# Revit family: Sanitary_Accessories_DURAVIT-AG_DuraSystem-Electronic-flush-plate-for-WC
name_source: partatom
category: Generic Models
revit_build: Autodesk Revit 2018 (Build: 20180329_1100(x64)
units: mm (PartAtom-declared; Revit-internal decimal feet)

## family parameters
Can host rebar = No
Cut with Voids When Loaded = No
Host = Face
OmniClass Number = 23.19.31.17
OmniClass Title = Sanitary Room Units
Part Type = Normal
Room Calculation Point = No
Round Connector Dimension = Use Diameter
Shared = No

## types (1)
- DuraSystem Electronic flush plate for WC 230x10x157 mm - WD5003
    BIMobject category = Bathroom Accessories
    Connector Description = Power input
    Date of publishing = 26.05.2020 00:00:00
    Default Elevation = 1219 mm
    Description = Duravit DuraSystem Electronic flush plate for WC 230x10x157 mm - WD5003012000
    Design country = Germany
    EAN code = 4053424507316
    ETIM classification = EC012353 | Accessories bathroom accessories
    Edition number = 1
    IFC Classification = Furnishing Element
    Installation instructions = https://pro.duravit.com
    Main material = Duravit - Metal - 00 - White Alpin
    Manufacturer = Duravit
    Manufacturer country = Germany
    Manufacturer name = DURAVIT AG
    Masterformat 2014 Code = 01 52 19
    Masterformat 2014 Description = Sanitary Facilities
    Material main = Glass
    Model = DuraSystem Electronic flush plate for WC 230x10x157 mm - WD5003
    NBS Reference Code = 35-93-62
    NBS Reference Description = Pre-Plumbed Installation Frames
    OmniClass Code = 23-19 31 17
    OmniClass Description = Sanitary Room Units
    Power = 0 A
    Product Guid = f8d118e6-736f-4f09-9c58-d784e3fbde4b
    Product SKU = DuraSystem-Electronic-flush-plate-for-WC--230x10x157-mm-WD5003
    Product certification = https://pro.duravit.com
    Product data url = https://bimobject.com
    Product family = DuraSystem
    Product group = Mechanical flush plate for WC
    Product name = DuraSystem Electronic flush plate for WC  230x10x157 mm - WD5003
    Product url = https://pro.duravit.com
    QR code = https://bimobject.com
    Technical description = https://pro.duravit.com
    UNSPSC Code = 301815
    URL = https://www.duravit.com
    Uniclass 1.4 Code = L7216
    Uniclass 1.4 Description = Toilets
    Uniclass 2.0 Code = PR-35-93-62
    Uniclass 2.0 Description = Pre-Plumbed Installation Frames
    Uniclass 2015 Code = Pr_40_20
    Uniclass 2015 Name = Sanitary fittings and accessories
    Uniformat II Code = D2010
    Uniformat II Description = Plumbing Fixtures
    Voltage = 24 V
    Weight Net (Kg) = 2.1
    Youtube clip = https://pro.duravit.com

## geometry (parser evidence)
native form markers: Sweep x4
no freeform markers — native parametric forms only
